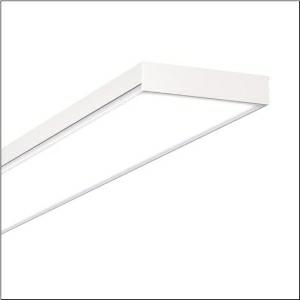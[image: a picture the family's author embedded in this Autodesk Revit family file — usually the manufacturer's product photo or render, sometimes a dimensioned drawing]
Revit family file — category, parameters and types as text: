
# Revit family: apollon_r__31_51mp26wm2341w_8243
name_source: partatom
category: Lighting Fixtures
units: mm (PartAtom-declared; Revit-internal decimal feet)

## family parameters
Cut with Voids When Loaded = No
Host = Face
Light Source = No
Part Type = Normal
Room Calculation Point = No
Round Connector Dimension = Use Diameter
Shared = No

## types (1)
- Apollon® 31 (1 x LED, 4400 lm, 33 W, 3000K)
    Apparent Load = 33 VA
    CIE Flux Codes = 61 87 97 97 100
    Color Rendering = 80
    Color Temperature = 3000K
    Default Elevation = 1800 mm
    Description = Apollon® 31, office luminaire, primary optical cover: micro prismatic cover, of PMMA, light emission: direct distribution, primary light characteristic: symmetric, installation type: surface-mounted, LED, rated luminous flux: 4.400lm, luminous efficacy: 133lm/W, light colour: 830, colour temperature: 3000K, control gear: ECG Multilumen, with terminal, 3-pole, mains connection: 220..240V, AC, 50/60Hz, rated input power: 33W, housing, of sheet steel, coil coated, traffic white (RAL 9016), length: 1.545mm, width: 200mm, height: 44mm, protection rating (complete): IP20, insulation class (complete): insulation class II (safety insulation), certification: CE, impact resistance: IK02, permissible operating ambient temperature: -20..+40°C, packaging unit: 1 piece
    Height = 44 mm
    Lamp = 1 x LED
    Lamp Light Flux = 4400 lm
    Lamp Power = 33 W
    Lamp count = 1
    Length = 1545 mm
    Luminous efficacy = 133 lm/W
    Manufacturer = Siteco
    ModVariant = No
    Model = 51MP26WM2341W
    Mounting Place = Ceiling
    Mounting Type = Surface mounted
    Number of Poles = 1
    OnlyDefault = Yes
    Power Factor = 1
    Product Name = Apollon® 31
    Product group = office luminaire | ceiling mounted
    ProductGroupID = 302
    Protection Class = Protection class II
    Protection Degree = IP 20
    RLX_Detail_Level = 1
    RlxData = <blob elided: 20729 chars, md5=04a83668>
    Socket = socket
    Standby Power = 0 W
    System Light Flux = 4400 lm
    System Power = 33 W
    Type Comments = Product without accessories
    Type Image = l_1007095.jpg
    URL = http://relux.com
    VarID = ---
    Voltage = 0 V
    Weight = 0.00 kg
    Width = 200 mm  [stored 0.656168 ft]

note: [stored X ft] marks values corroborated as IEEE doubles in the binary element streams (Revit-internal decimal feet)

## geometry (parser evidence)
native form markers: Blend x4, Sweep x10
no freeform markers — native parametric forms only
